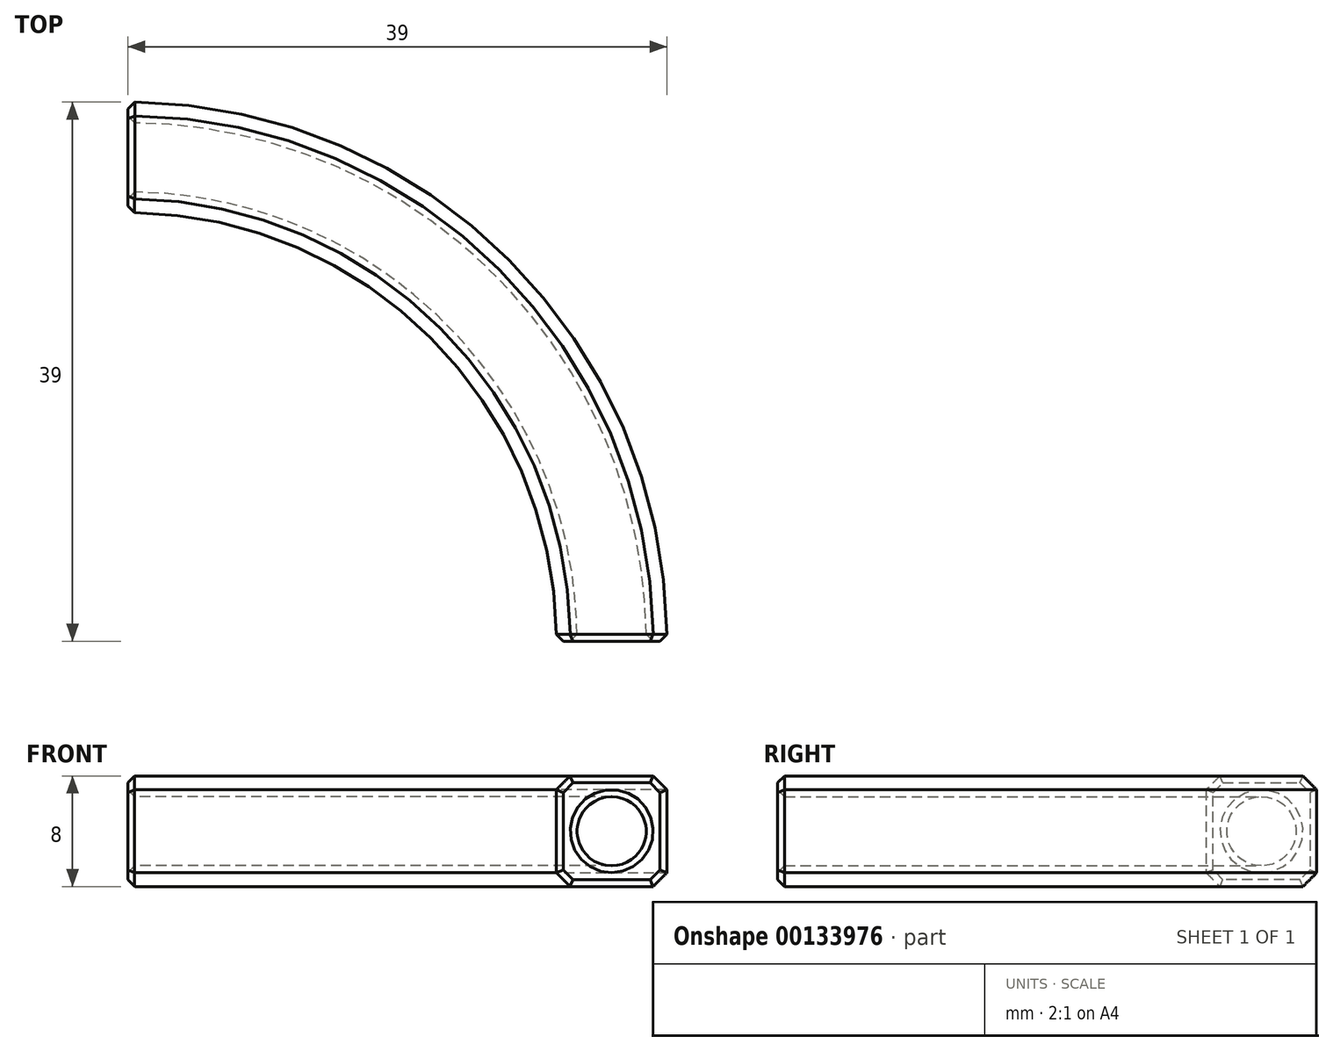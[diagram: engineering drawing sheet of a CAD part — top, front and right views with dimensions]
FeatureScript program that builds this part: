
annotation { "Feature Type Name" : "Feature", "Feature Type Description" : "" }
export const myFeature = defineFeature(function(context is Context, id is Id, definition is map)
    precondition{}
    {
        {
            var Q0;
            Q0=qCreatedBy(makeId("Top.planeOp"),FACE);
            var sketch = newSketch(context, id + "F0", { "sketchPlane" : qUnion([Q0])});
            skArc(sketch, "E0", {"start": v(35, 0) * mm, "mid": v(24.75, 24.75) * mm, "end": v(0, 35) * mm});
            skSolve(sketch);
        }
        {
            var Q0;
            Q0=qCreatedBy(makeId("Right.planeOp"),FACE);
            var sketch = newSketch(context, id + "F1", { "sketchPlane" : qUnion([Q0])});
            skLineSegment(sketch, "E1.bottom", {"start": v(31, -4) * mm, "end": v(39, -4) * mm});
            skLineSegment(sketch, "E1.top", {"start": v(31, 4) * mm, "end": v(39, 4) * mm});
            skLineSegment(sketch, "E1.left", {"start": v(31, -4) * mm, "end": v(31, 4) * mm});
            skLineSegment(sketch, "E1.right", {"start": v(39, -4) * mm, "end": v(39, 4) * mm});
            skPoint(sketch, "E1.middle", {"position": v(35, 0) * mm});
            skCircle(sketch, "E2", {"center": v(35, 0) * mm, "radius": 2.5 * mm});
            skSolve(sketch);
        }
        {
            var Q0;
            Q0 = qSketchRegion(id + "F1", true);
            var Q1;
            Q1 = qConstructionFilter(qBodyType(qCreatedBy(id + "F0" ,EDGE), BodyType.WIRE), ConstructionObject.NO);
            sweep(context, id + "F2", {"profiles" : qUnion([Q0]), "path" : qUnion([Q1])});
        }
        {
            var Q0;
            Q0=makeQuery(id+"F2.opSweep","SWEPT_EDGE",EDGE,{"disambiguationData":[OSD([sQuery(id+"F0.wireOp",EDGE,"E0"),sQuery(id+"F1.wireOp",EDGE,"E1.top"),sQuery(id+"F1.wireOp",EDGE,"E1.left")])]});
            var Q1;
            Q1=makeQuery(id+"F2.opSweep","SWEPT_EDGE",EDGE,{"disambiguationData":[OSD([sQuery(id+"F0.wireOp",EDGE,"E0"),sQuery(id+"F1.wireOp",EDGE,"E1.top"),sQuery(id+"F1.wireOp",EDGE,"E1.right")])]});
            var Q2;
            Q2=makeQuery(id+"F2.opSweep","SWEPT_EDGE",EDGE,{"disambiguationData":[OSD([sQuery(id+"F0.wireOp",EDGE,"E0"),sQuery(id+"F1.wireOp",EDGE,"E1.bottom"),sQuery(id+"F1.wireOp",EDGE,"E1.left")])]});
            var Q3;
            Q3=makeQuery(id+"F2.opSweep","SWEPT_EDGE",EDGE,{"disambiguationData":[OSD([sQuery(id+"F0.wireOp",EDGE,"E0"),sQuery(id+"F1.wireOp",EDGE,"E1.bottom"),sQuery(id+"F1.wireOp",EDGE,"E1.right")])]});
            chamfer(context, id + "F3", {"entities" : qUnion([Q0, Q1, Q2, Q3]), "width" : 1 * mm, "tangentPropagation" : true});
        }
        {
            var Q0;
            Q0=makeQuery(id+"F2.opSweep","CAP_FACE",FACE,{"disambiguationData":[OSD([sQuery(id+"F0.wireOp",VERTEX,"E0.end"),sQuery(id+"F1.wireOp",EDGE,"E1.bottom"),sQuery(id+"F1.wireOp",EDGE,"E1.top"),sQuery(id+"F1.wireOp",EDGE,"E1.left"),sQuery(id+"F1.wireOp",EDGE,"E1.right"),sQuery(id+"F1.wireOp",EDGE,"E2")])],"isStart":true});
            var Q1;
            Q1=makeQuery(id+"F2.opSweep","CAP_FACE",FACE,{"disambiguationData":[OSD([sQuery(id+"F0.wireOp",VERTEX,"E0.start"),sQuery(id+"F1.wireOp",EDGE,"E1.bottom"),sQuery(id+"F1.wireOp",EDGE,"E1.top"),sQuery(id+"F1.wireOp",EDGE,"E1.left"),sQuery(id+"F1.wireOp",EDGE,"E1.right"),sQuery(id+"F1.wireOp",EDGE,"E2")])],"isStart":false});
            chamfer(context, id + "F4", {"entities" : qUnion([Q0, Q1]), "width" : 0.5 * mm, "tangentPropagation" : true});
        }
    });
